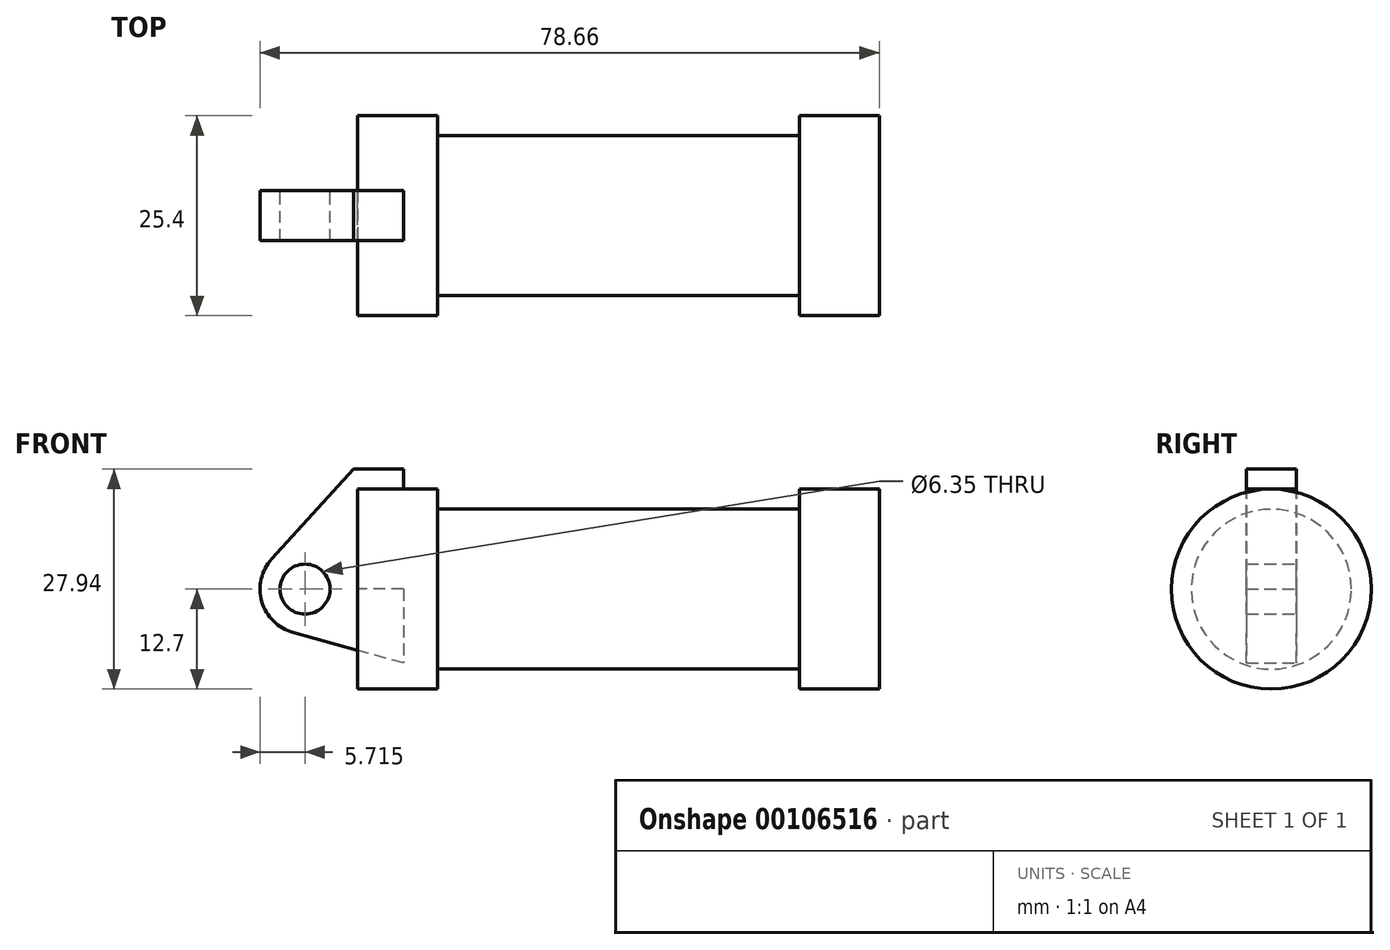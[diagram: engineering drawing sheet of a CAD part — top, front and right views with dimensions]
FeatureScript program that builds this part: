
annotation { "Feature Type Name" : "Feature", "Feature Type Description" : "" }
export const myFeature = defineFeature(function(context is Context, id is Id, definition is map)
    precondition{}
    {
        {
            var Q0;
            Q0=qCreatedBy(makeId("Front.planeOp"),FACE);
            var sketch = newSketch(context, id + "F0", { "sketchPlane" : qUnion([Q0])});
            skLineSegment(sketch, "E0", {"start": v(0, 0) * mm, "end": v(0, 12.7) * mm});
            skLineSegment(sketch, "E1", {"start": v(0, 12.7) * mm, "end": v(10.16, 12.7) * mm});
            skLineSegment(sketch, "E2", {"start": v(10.16, 12.7) * mm, "end": v(10.16, 10.16) * mm});
            skLineSegment(sketch, "E3", {"start": v(10.16, 10.16) * mm, "end": v(56.13, 10.16) * mm});
            skLineSegment(sketch, "E4", {"start": v(56.13, 10.16) * mm, "end": v(56.13, 12.7) * mm});
            skLineSegment(sketch, "E5", {"start": v(56.13, 12.7) * mm, "end": v(66.3, 12.7) * mm});
            skLineSegment(sketch, "E6", {"start": v(66.3, 12.7) * mm, "end": v(66.3, 0) * mm});
            skLineSegment(sketch, "E7", {"start": v(66.3, 0) * mm, "end": v(0, 0) * mm});
            skLineSegment(sketch, "E8", {"start": v(5.84, 15.24) * mm, "end": v(-0.5, 15.24) * mm});
            skLineSegment(sketch, "E9", {"start": v(-0.5, 15.24) * mm, "end": v(-10.88, 3.85) * mm});
            skLineSegment(sketch, "E10", {"start": v(0, 0) * mm, "end": v(-6.65, 0) * mm});
            skCircle(sketch, "E11", {"center": v(-6.65, 0) * mm, "radius": 5.72 * mm});
            skCircle(sketch, "E12", {"center": v(-6.65, 0) * mm, "radius": 3.18 * mm});
            skLineSegment(sketch, "E13", {"start": v(5.84, 15.24) * mm, "end": v(5.84, -9.4) * mm});
            skLineSegment(sketch, "E14", {"start": v(5.84, -9.4) * mm, "end": v(-8.18, -5.5) * mm});
            skSolve(sketch);
        }
        {
            var Q0;
            {var subQ0=sQuery(id+"F0.wireOp",EDGE,"E2");Q0=makeQuery(id+"F0.imprint","IMPRINT",FACE,{"disambiguationData":[TD([[makeQuery(id+"F0.imprint","IMPRINT",EDGE,{"derivedFrom":subQ0}),-1.0]])]});}
            var Q1;
            {var subQ0=sQuery(id+"F0.wireOp",EDGE,"E0");Q1=makeQuery(id+"F0.imprint","IMPRINT",FACE,{"disambiguationData":[TD([[makeQuery(id+"F0.imprint","IMPRINT",EDGE,{"derivedFrom":subQ0}),-1.0]])]});}
            var Q2;
            Q2=sQuery(id+"F0.wireOp",EDGE,"E7");
            revolve(context, id + "F1", {"entities" : qUnion([Q0, Q1]), "axis" : qUnion([Q2]), "revolveType" : RevolveType.FULL});
        }
        {
            var Q0;
            {var subQ3=sQuery(id+"F0.wireOp",EDGE,"E0");Q0=makeQuery(id+"F0.imprint","IMPRINT",FACE,{"disambiguationData":[TD([[makeQuery(id+"F0.imprint","IMPRINT",EDGE,{"derivedFrom":subQ3}),1.0]])]});}
            var Q1;
            {var subQ4=sQuery(id+"F0.wireOp",EDGE,"E12");Q1=makeQuery(id+"F0.imprint","IMPRINT",FACE,{"disambiguationData":[TD([[makeQuery(id+"F0.imprint","IMPRINT",EDGE,{"derivedFrom":subQ4}),-1.0]])]});}
            var Q2;
            {var subQ0=sQuery(id+"F0.wireOp",EDGE,"E14");Q2=makeQuery(id+"F0.imprint","IMPRINT",FACE,{"disambiguationData":[TD([[makeQuery(id+"F0.imprint","IMPRINT",EDGE,{"derivedFrom":subQ0}),-1.0]])]});}
            extrude(context, id + "F2", {"entities" : qUnion([Q0, Q1, Q2]), "endBound" : BoundingType.SYMMETRIC, "depth" : 6.35 * mm});
        }
    });
